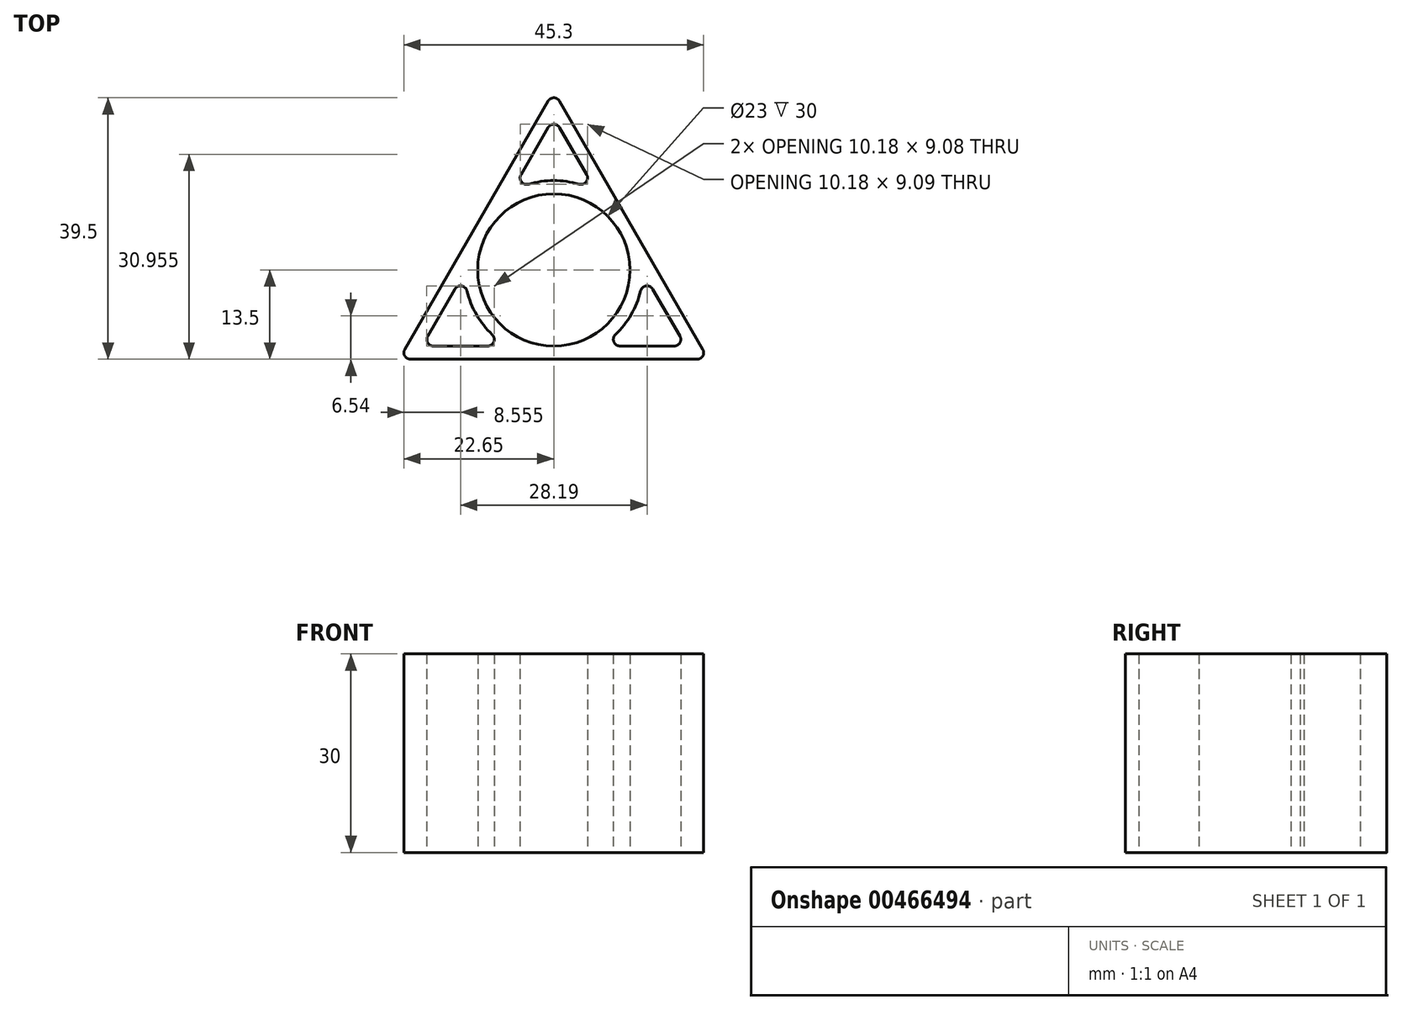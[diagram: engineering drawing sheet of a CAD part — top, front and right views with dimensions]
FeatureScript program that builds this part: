
annotation { "Feature Type Name" : "Feature", "Feature Type Description" : "" }
export const myFeature = defineFeature(function(context is Context, id is Id, definition is map)
    precondition{}
    {
        {
            var Q0;
            Q0=qCreatedBy(makeId("Top.planeOp"),FACE);
            var sketch = newSketch(context, id + "F0", { "sketchPlane" : qUnion([Q0])});
            skCircle(sketch, "E0.cCircle", {"center": v(0, 0) * mm, "radius": 27 * mm, "construction": true});
            skLineSegment(sketch, "E0.0", {"start": v(0.87, 25.5) * mm, "end": v(11.7, 6.75) * mm});
            skLineSegment(sketch, "E0.1", {"start": v(21.65, -13.5) * mm, "end": v(-21.65, -13.5) * mm});
            skLineSegment(sketch, "E0.2", {"start": v(-22.52, -12) * mm, "end": v(-0.87, 25.5) * mm});
            skLineSegment(sketch, "E1.0", {"start": v(-19.05, -10) * mm, "end": v(-14.96, -2.91) * mm});
            skLineSegment(sketch, "E1.1", {"start": v(18.19, -11.5) * mm, "end": v(10, -11.5) * mm});
            skLineSegment(sketch, "E1.2", {"start": v(0.87, 21.5) * mm, "end": v(4.96, 14.41) * mm});
            skCircle(sketch, "E2.0", {"center": v(0, 0) * mm, "radius": 11.5 * mm});
            skLineSegment(sketch, "E3", {"start": v(6.42, 11.87) * mm, "end": v(13.5, -0.37) * mm, "construction": true});
            skLineSegment(sketch, "E4", {"start": v(14.96, -2.91) * mm, "end": v(19.05, -10) * mm});
            skLineSegment(sketch, "E5", {"start": v(11.7, 6.75) * mm, "end": v(22.52, -12) * mm});
            skArc(sketch, "E6", {"start": v(3.81, 12.95) * mm, "mid": v(0, 13.5) * mm, "end": v(-3.81, 12.95) * mm});
            skArc(sketch, "E7", {"start": v(13.5, -0.37) * mm, "mid": v(11.7, 6.75) * mm, "end": v(6.42, 11.87) * mm, "construction": true});
            skLineSegment(sketch, "E8", {"start": v(-4.96, 14.41) * mm, "end": v(-0.87, 21.5) * mm});
            skLineSegment(sketch, "E9", {"start": v(-13.5, -0.37) * mm, "end": v(-6.42, 11.87) * mm, "construction": true});
            skArc(sketch, "E10", {"start": v(-6.42, 11.87) * mm, "mid": v(-11.7, 6.75) * mm, "end": v(-13.5, -0.37) * mm, "construction": true});
            skArc(sketch, "E11", {"start": v(-13.12, -3.18) * mm, "mid": v(-11.7, -6.75) * mm, "end": v(-9.31, -9.78) * mm});
            skLineSegment(sketch, "E12", {"start": v(-10, -11.5) * mm, "end": v(-18.19, -11.5) * mm});
            skLineSegment(sketch, "E13", {"start": v(7.07, -11.5) * mm, "end": v(-7.07, -11.5) * mm, "construction": true});
            skArc(sketch, "E14", {"start": v(9.31, -9.78) * mm, "mid": v(11.7, -6.75) * mm, "end": v(13.12, -3.18) * mm});
            skArc(sketch, "E15", {"start": v(-7.07, -11.5) * mm, "mid": v(0, -13.5) * mm, "end": v(7.07, -11.5) * mm, "construction": true});
            skPoint(sketch, "E16.visualSharp", {"position": v(0, 27) * mm});
            skArc(sketch, "E16.filletArc", {"start": v(0.87, 25.5) * mm, "mid": v(0, 26) * mm, "end": v(-0.87, 25.5) * mm});
            skCircle(sketch, "E17", {"center": v(0, 0) * mm, "radius": 26 * mm, "construction": true});
            skPoint(sketch, "E18.visualSharp", {"position": v(23.38, -13.5) * mm});
            skArc(sketch, "E18.filletArc", {"start": v(21.65, -13.5) * mm, "mid": v(22.52, -13) * mm, "end": v(22.52, -12) * mm});
            skPoint(sketch, "E19.visualSharp", {"position": v(-23.38, -13.5) * mm});
            skArc(sketch, "E19.filletArc", {"start": v(-22.52, -12) * mm, "mid": v(-22.52, -13) * mm, "end": v(-21.65, -13.5) * mm});
            skPoint(sketch, "E20.visualSharp", {"position": v(-19.92, -11.5) * mm});
            skArc(sketch, "E20.filletArc", {"start": v(-19.05, -10) * mm, "mid": v(-19.05, -11) * mm, "end": v(-18.19, -11.5) * mm});
            skPoint(sketch, "E21.visualSharp", {"position": v(19.92, -11.5) * mm});
            skArc(sketch, "E21.filletArc", {"start": v(18.19, -11.5) * mm, "mid": v(19.05, -11) * mm, "end": v(19.05, -10) * mm});
            skPoint(sketch, "E22.visualSharp", {"position": v(0, 23) * mm});
            skArc(sketch, "E22.filletArc", {"start": v(0.87, 21.5) * mm, "mid": v(0, 22) * mm, "end": v(-0.87, 21.5) * mm});
            skPoint(sketch, "E23.visualSharp", {"position": v(-13.5, -0.37) * mm});
            skArc(sketch, "E23.filletArc", {"start": v(-13.12, -3.18) * mm, "mid": v(-13.95, -2.42) * mm, "end": v(-14.96, -2.91) * mm});
            skPoint(sketch, "E24.visualSharp", {"position": v(-7.07, -11.5) * mm});
            skArc(sketch, "E24.filletArc", {"start": v(-10, -11.5) * mm, "mid": v(-9.07, -10.87) * mm, "end": v(-9.31, -9.78) * mm});
            skPoint(sketch, "E25.visualSharp", {"position": v(7.07, -11.5) * mm});
            skArc(sketch, "E25.filletArc", {"start": v(9.31, -9.78) * mm, "mid": v(9.07, -10.87) * mm, "end": v(10, -11.5) * mm});
            skPoint(sketch, "E26.visualSharp", {"position": v(13.5, -0.37) * mm});
            skArc(sketch, "E26.filletArc", {"start": v(14.96, -2.91) * mm, "mid": v(13.95, -2.42) * mm, "end": v(13.12, -3.18) * mm});
            skPoint(sketch, "E27.visualSharp", {"position": v(6.42, 11.87) * mm});
            skArc(sketch, "E27.filletArc", {"start": v(3.81, 12.95) * mm, "mid": v(4.88, 13.3) * mm, "end": v(4.96, 14.41) * mm});
            skPoint(sketch, "E28.visualSharp", {"position": v(-6.42, 11.87) * mm});
            skArc(sketch, "E28.filletArc", {"start": v(-4.96, 14.41) * mm, "mid": v(-4.88, 13.3) * mm, "end": v(-3.81, 12.95) * mm});
            skSolve(sketch);
        }
        {
            var Q0;
            Q0=makeQuery(id+"F0.imprint","IMPRINT",FACE,{"disambiguationData":[TD([[makeQuery(id+"F0.imprint","IMPRINT",EDGE,{"derivedFrom":sQuery(id+"F0.wireOp",EDGE,"E0.0")}),-1.0]])]});
            extrude(context, id + "F1", {"entities" : qUnion([Q0]), "depth" : 30 * mm});
        }
    });
